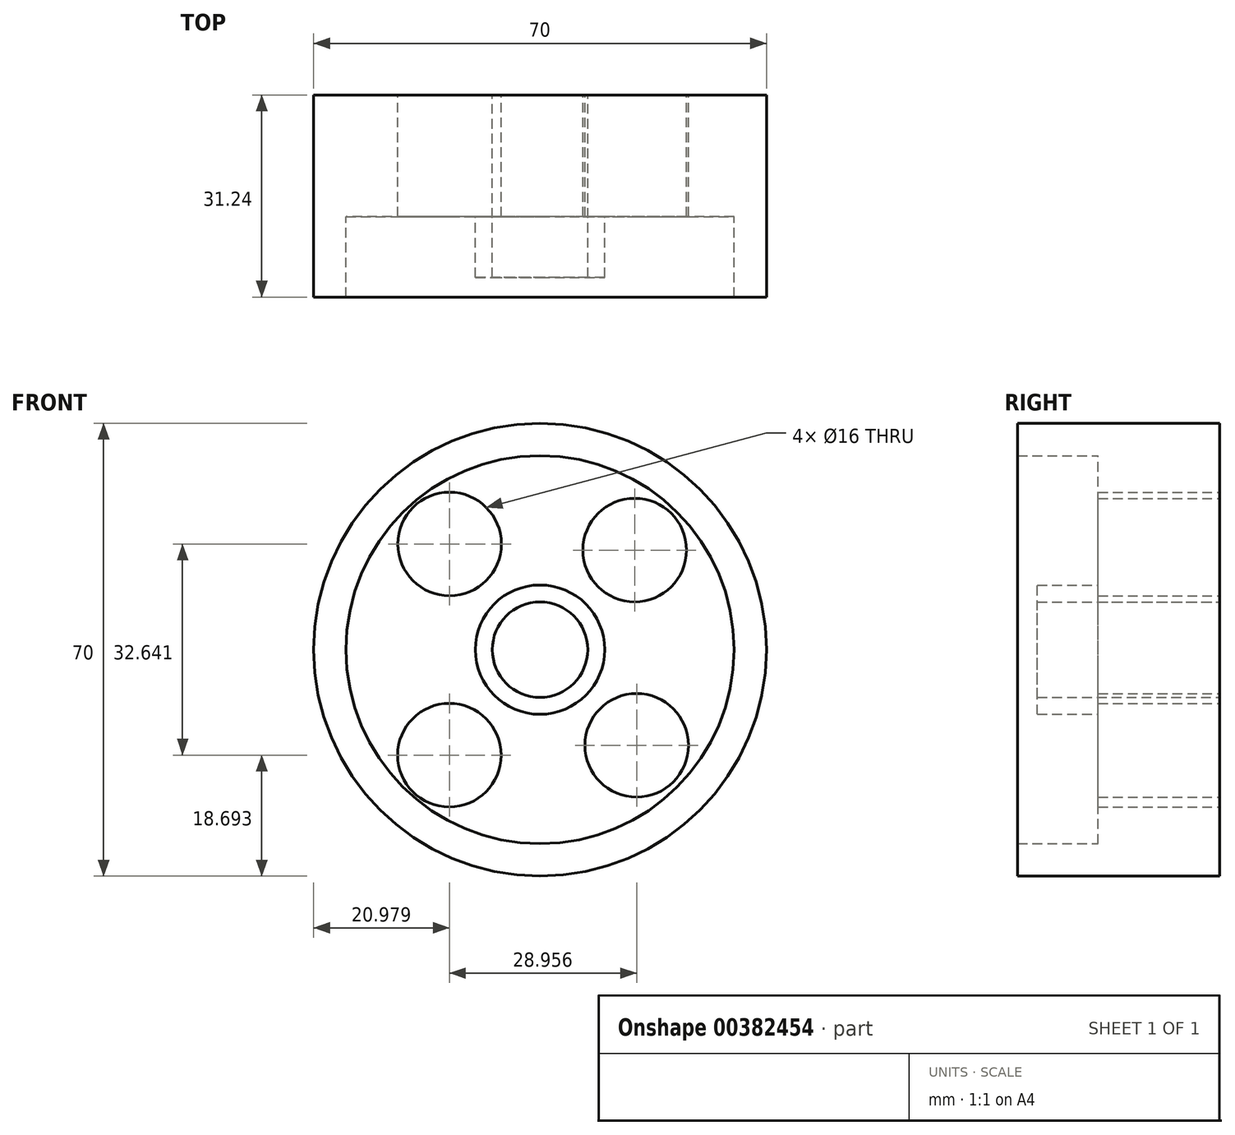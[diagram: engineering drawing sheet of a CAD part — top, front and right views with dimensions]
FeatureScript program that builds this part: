
annotation { "Feature Type Name" : "Feature", "Feature Type Description" : "" }
export const myFeature = defineFeature(function(context is Context, id is Id, definition is map)
    precondition{}
    {
        {
            var Q0;
            Q0=qCreatedBy(makeId("Front.planeOp"),FACE);
            var sketch = newSketch(context, id + "F0", { "sketchPlane" : qUnion([Q0])});
            skCircle(sketch, "E0", {"center": v(0, 0) * mm, "radius": 35 * mm});
            skCircle(sketch, "E1", {"center": v(0, 0) * mm, "radius": 30 * mm});
            skCircle(sketch, "E2", {"center": v(0, 0) * mm, "radius": 10 * mm});
            skCircle(sketch, "E3", {"center": v(-13.98, 16.33) * mm, "radius": 8 * mm});
            skCircle(sketch, "E4", {"center": v(-14.02, -16.3) * mm, "radius": 8 * mm});
            skCircle(sketch, "E5", {"center": v(14.94, -14.78) * mm, "radius": 8 * mm});
            skCircle(sketch, "E6", {"center": v(14.63, 15.4) * mm, "radius": 8 * mm});
            skCircle(sketch, "E7", {"center": v(0, 0) * mm, "radius": 7.38 * mm});
            skSolve(sketch);
        }
        {
            var Q0;
            Q0 = qSketchRegion(id + "F0", true);
            extrude(context, id + "F1", {"entities" : qUnion([Q0]), "depth" : 31.24 * mm});
        }
        {
            var Q0;
            Q0=makeQuery(id+"F0.imprint","IMPRINT",FACE,{"disambiguationData":[TD([[makeQuery(id+"F0.imprint","IMPRINT",EDGE,{"derivedFrom":sQuery(id+"F0.wireOp",EDGE,"E1")}),1.0]])]});
            extrude(context, id + "F2", {"entities" : qUnion([Q0]), "operationType" : NewBodyOperationType.ADD, "depth" : 18.8 * mm});
        }
        {
            var Q0;
            Q0=makeQuery(id+"F0.imprint","IMPRINT",FACE,{"disambiguationData":[TD([[makeQuery(id+"F0.imprint","IMPRINT",EDGE,{"derivedFrom":sQuery(id+"F0.wireOp",EDGE,"E2")}),1.0]])]});
            extrude(context, id + "F3", {"entities" : qUnion([Q0]), "operationType" : NewBodyOperationType.ADD, "depth" : 28.2 * mm});
        }
    });
